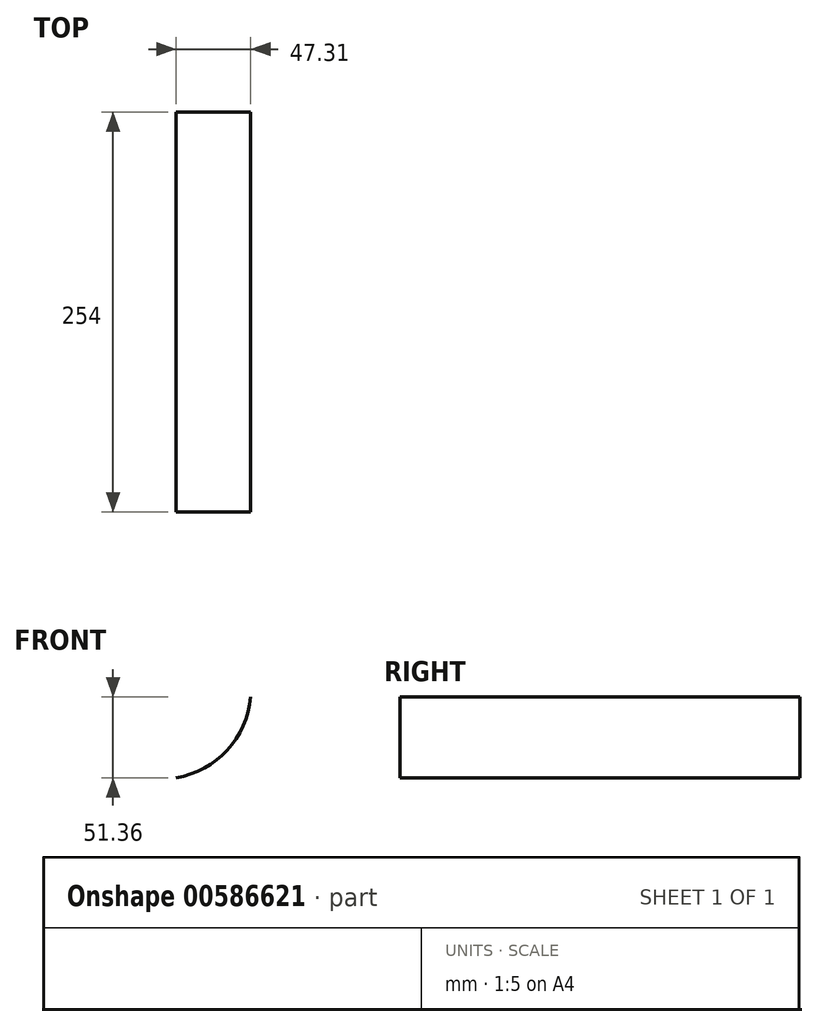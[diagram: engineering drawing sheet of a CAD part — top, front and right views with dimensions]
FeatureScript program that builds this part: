
annotation { "Feature Type Name" : "Feature", "Feature Type Description" : "" }
export const myFeature = defineFeature(function(context is Context, id is Id, definition is map)
    precondition{}
    {
        {
            var Q0;
            Q0=qCreatedBy(makeId("Front.planeOp"),FACE);
            var sketch = newSketch(context, id + "F0", { "sketchPlane" : qUnion([Q0])});
            skArc(sketch, "E0", {"start": v(-50.75, -62.68) * mm, "mid": v(-18.28, -45.12) * mm, "end": v(-3.44, -11.32) * mm});
            skSolve(sketch);
        }
        {
            var Q0;
            Q0 = qSketchRegion(id + "F0", true);
            var Q1;
            Q1=sQuery(id+"F0.wireOp",EDGE,"E0");
            extrude(context, id + "F1", {"entities" : qUnion([Q0]), "bodyType" : ToolBodyType.SURFACE, "surfaceEntities" : qUnion([Q1]), "endBound" : BoundingType.SYMMETRIC, "depth" : 254 * mm, "offsetDistance" : 25.4 * mm});
        }
    });
